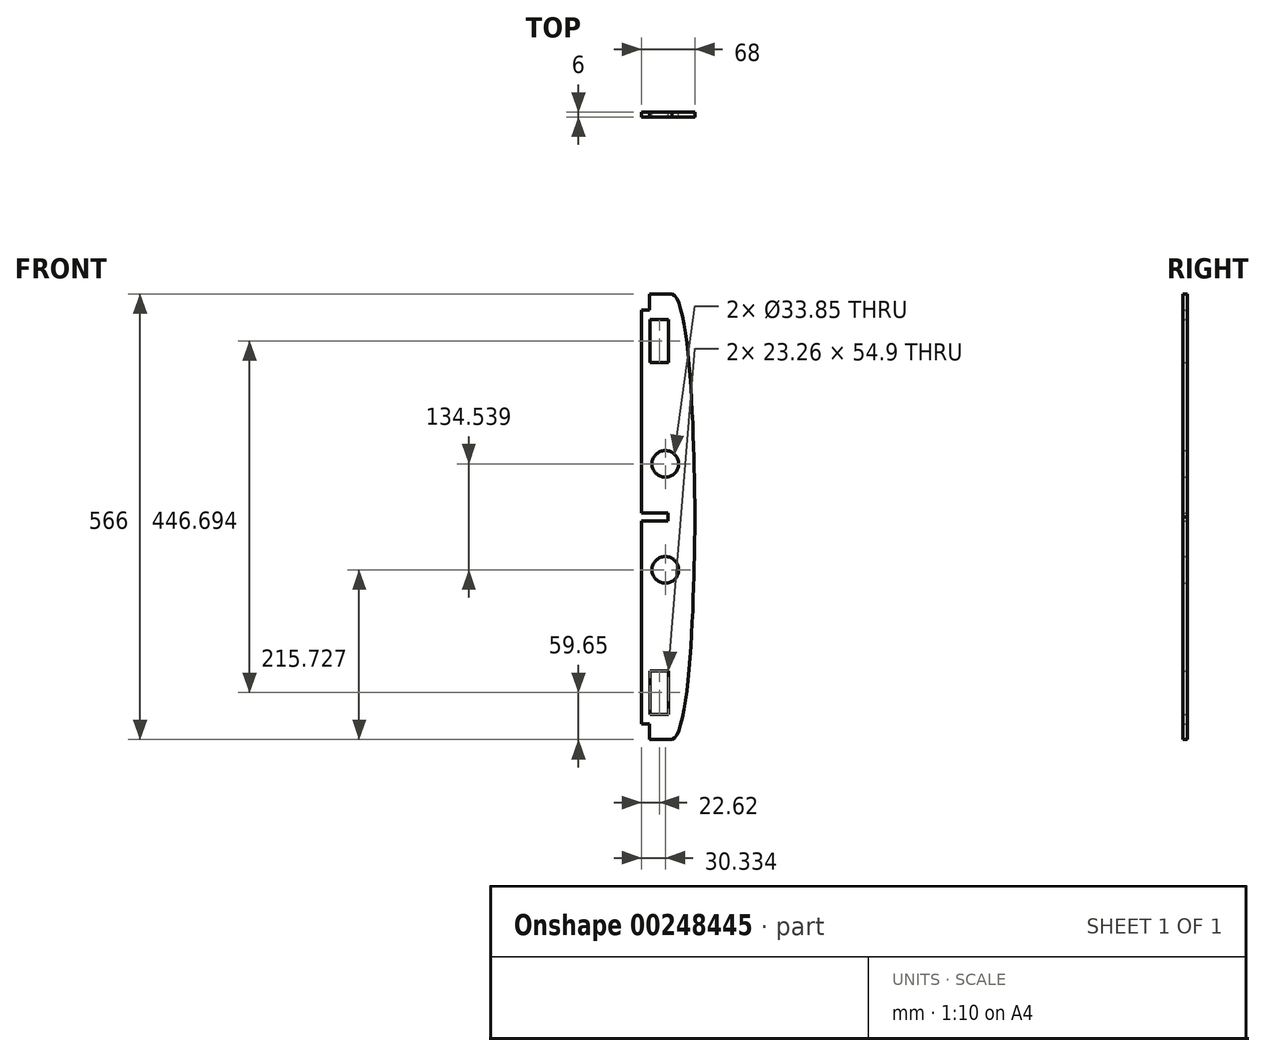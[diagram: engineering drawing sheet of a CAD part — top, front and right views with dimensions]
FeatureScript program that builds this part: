
annotation { "Feature Type Name" : "Feature", "Feature Type Description" : "" }
export const myFeature = defineFeature(function(context is Context, id is Id, definition is map)
    precondition{}
    {
        {
            var Q0;
            Q0=qCreatedBy(makeId("Front.planeOp"),FACE);
            var sketch = newSketch(context, id + "F0", { "sketchPlane" : qUnion([Q0])});
            skLineSegment(sketch, "E0.top", {"start": v(266.3, 129.32) * mm, "end": v(208.5, 129.32) * mm});
            skFitSpline(sketch, "E1", {"points": [v(237.5, 129.32) * mm, v(266.5, -153.68) * mm], "startDerivative": vector(86.43, -25.5) * mm, "endDerivative": vector(0.57, -6.3) * mm});
            skLineSegment(sketch, "E2", {"start": v(266.5, -153.68) * mm, "end": v(198.5, -153.68) * mm});
            skLineSegment(sketch, "E3", {"start": v(266.3, 129.32) * mm, "end": v(266.3, -151.58) * mm});
            skLineSegment(sketch, "E4.bottom", {"start": v(232.75, 97.11) * mm, "end": v(209.49, 97.11) * mm});
            skLineSegment(sketch, "E4.top", {"start": v(232.75, 42.21) * mm, "end": v(209.49, 42.21) * mm});
            skLineSegment(sketch, "E4.left", {"start": v(232.75, 97.11) * mm, "end": v(232.75, 42.21) * mm});
            skLineSegment(sketch, "E4.right", {"start": v(209.49, 97.11) * mm, "end": v(209.49, 42.21) * mm});
            skCircle(sketch, "E5", {"center": v(228.83, -86.41) * mm, "radius": 16.93 * mm});
            skLineSegment(sketch, "E6.MirrorCS", {"start": v(232.75, -349.58) * mm, "end": v(209.49, -349.58) * mm});
            skLineSegment(sketch, "E7.MirrorCS", {"start": v(209.49, -404.48) * mm, "end": v(209.49, -349.58) * mm});
            skFitSpline(sketch, "E8.MirrorCS", {"points": [v(237.5, -436.68) * mm, v(266.5, -153.68) * mm], "startDerivative": vector(86.43, 25.5) * mm, "endDerivative": vector(0.57, 6.3) * mm});
            skLineSegment(sketch, "E9.MirrorCS", {"start": v(266.3, -436.68) * mm, "end": v(208.5, -436.68) * mm});
            skLineSegment(sketch, "E10.MirrorCS", {"start": v(232.75, -404.48) * mm, "end": v(209.49, -404.48) * mm});
            skLineSegment(sketch, "E11.MirrorCS", {"start": v(266.3, -436.68) * mm, "end": v(266.3, -155.78) * mm});
            skLineSegment(sketch, "E12.MirrorCS", {"start": v(232.75, -404.48) * mm, "end": v(232.75, -349.58) * mm});
            skCircle(sketch, "E13.MirrorC", {"center": v(228.83, -220.95) * mm, "radius": 16.93 * mm});
            skLineSegment(sketch, "E14", {"start": v(232.5, -153.68) * mm, "end": v(232.5, -148.68) * mm});
            skLineSegment(sketch, "E15", {"start": v(232.5, -153.68) * mm, "end": v(232.5, -158.68) * mm});
            skLineSegment(sketch, "E16", {"start": v(232.5, -148.68) * mm, "end": v(198.5, -148.68) * mm});
            skLineSegment(sketch, "E17", {"start": v(232.5, -158.68) * mm, "end": v(198.5, -158.68) * mm});
            skLineSegment(sketch, "E18", {"start": v(208.5, 129.32) * mm, "end": v(208.5, 109.32) * mm});
            skLineSegment(sketch, "E19", {"start": v(208.5, 109.32) * mm, "end": v(198.5, 109.32) * mm});
            skLineSegment(sketch, "E20", {"start": v(208.5, 129.32) * mm, "end": v(237.5, 129.32) * mm});
            skLineSegment(sketch, "E21", {"start": v(198.5, 109.32) * mm, "end": v(198.5, -153.68) * mm});
            skLineSegment(sketch, "E22.MirrorCS", {"start": v(208.5, -436.68) * mm, "end": v(208.5, -416.68) * mm});
            skLineSegment(sketch, "E23.MirrorCS", {"start": v(208.5, -416.68) * mm, "end": v(198.5, -416.68) * mm});
            skLineSegment(sketch, "E24", {"start": v(198.5, -416.68) * mm, "end": v(198.5, -153.68) * mm});
            skLineSegment(sketch, "E25", {"start": v(208.5, -436.68) * mm, "end": v(237.5, -436.68) * mm});
            skSolve(sketch);
        }
        {
            var Q0;
            {var subQ3=sQuery(id+"F0.wireOp",EDGE,"f6c7303f-daa8-469b-b25b-95339dbf5836");Q0=makeQuery(id+"F0.imprint","IMPRINT",FACE,{"disambiguationData":[TD([[makeQuery(id+"F0.imprint","IMPRINT",EDGE,{"derivedFrom":subQ3}),-1.0]])]});}
            var Q1;
            Q1=makeQuery(id+"F0.imprint","IMPRINT",FACE,{"disambiguationData":[TD([[makeQuery(id+"F0.imprint","IMPRINT",EDGE,{"derivedFrom":sQuery(id+"F0.wireOp",EDGE,"E6.MirrorCS")}),-1.0]])]});
            var Q2;
            Q2=makeQuery(id+"F0.imprint","IMPRINT",FACE,{"disambiguationData":[TD([[makeQuery(id+"F0.imprint","IMPRINT",EDGE,{"derivedFrom":sQuery(id+"F0.wireOp",EDGE,"E4.bottom")}),-1.0]])]});
            extrude(context, id + "F1", {"entities" : qUnion([Q0, Q1, Q2]), "depth" : 6 * mm});
        }
    });
